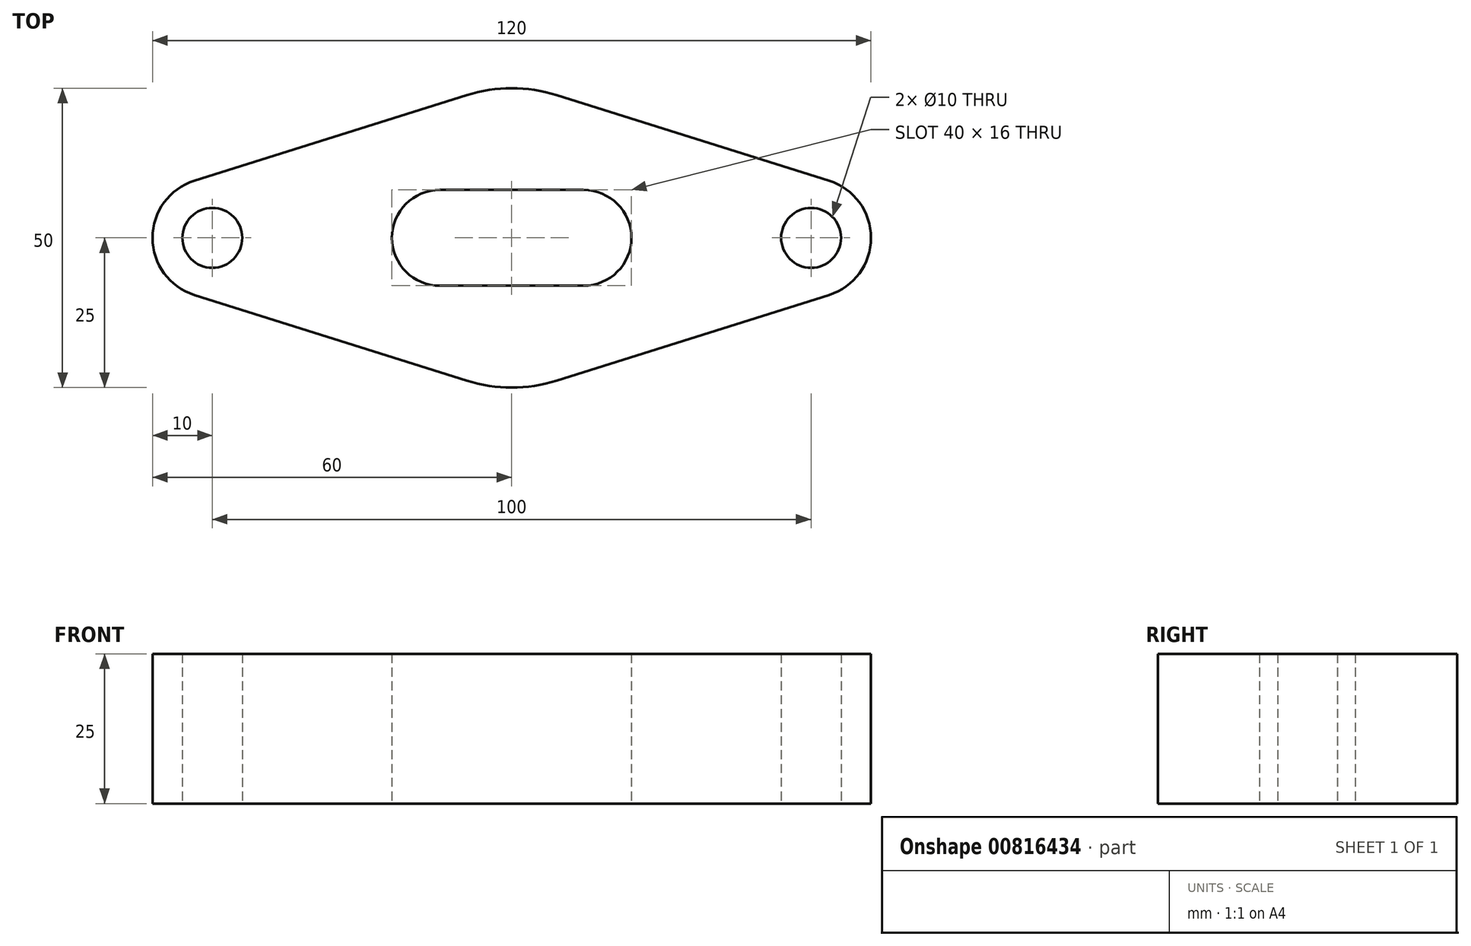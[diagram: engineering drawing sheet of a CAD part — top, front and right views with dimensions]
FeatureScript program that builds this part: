
annotation { "Feature Type Name" : "Feature", "Feature Type Description" : "" }
export const myFeature = defineFeature(function(context is Context, id is Id, definition is map)
    precondition{}
    {
        {
            var Q0;
            Q0=qCreatedBy(makeId("Top.planeOp"),FACE);
            var sketch = newSketch(context, id + "F0", { "sketchPlane" : qUnion([Q0])});
            skArc(sketch, "E0", {"start": v(-7.5, -23.85) * mm, "mid": v(0, -25) * mm, "end": v(7.5, -23.85) * mm});
            skCircle(sketch, "E1", {"center": v(50, 0) * mm, "radius": 10 * mm});
            skCircle(sketch, "E2", {"center": v(-50, 0) * mm, "radius": 10 * mm});
            skLineSegment(sketch, "E3", {"start": v(-53, 9.54) * mm, "end": v(-7.5, 23.85) * mm});
            skLineSegment(sketch, "E4", {"start": v(7.5, 23.85) * mm, "end": v(53, 9.54) * mm});
            skLineSegment(sketch, "E5", {"start": v(-53, -9.54) * mm, "end": v(-7.5, -23.85) * mm});
            skLineSegment(sketch, "E6", {"start": v(53, -9.54) * mm, "end": v(7.5, -23.85) * mm});
            skCircle(sketch, "E7", {"center": v(-50, 0) * mm, "radius": 5 * mm});
            skCircle(sketch, "E8", {"center": v(50, 0) * mm, "radius": 5 * mm});
            skArc(sketch, "E9.trimOffspring", {"start": v(7.5, 23.85) * mm, "mid": v(0, 25) * mm, "end": v(-7.5, 23.85) * mm});
            skArc(sketch, "E10", {"start": v(12, -8) * mm, "mid": v(20, 0) * mm, "end": v(12, 8) * mm});
            skArc(sketch, "E11", {"start": v(-12, 8) * mm, "mid": v(-20, 0) * mm, "end": v(-12, -8) * mm});
            skLineSegment(sketch, "E12", {"start": v(-12, 8) * mm, "end": v(12, 8) * mm});
            skLineSegment(sketch, "E13", {"start": v(-12, -8) * mm, "end": v(12, -8) * mm});
            skSolve(sketch);
        }
        {
            var Q0;
            Q0 = qSketchRegion(id + "F0", true);
            extrude(context, id + "F1", {"entities" : qUnion([Q0]), "depth" : 25 * mm, "offsetDistance" : 25 * mm});
        }
    });
